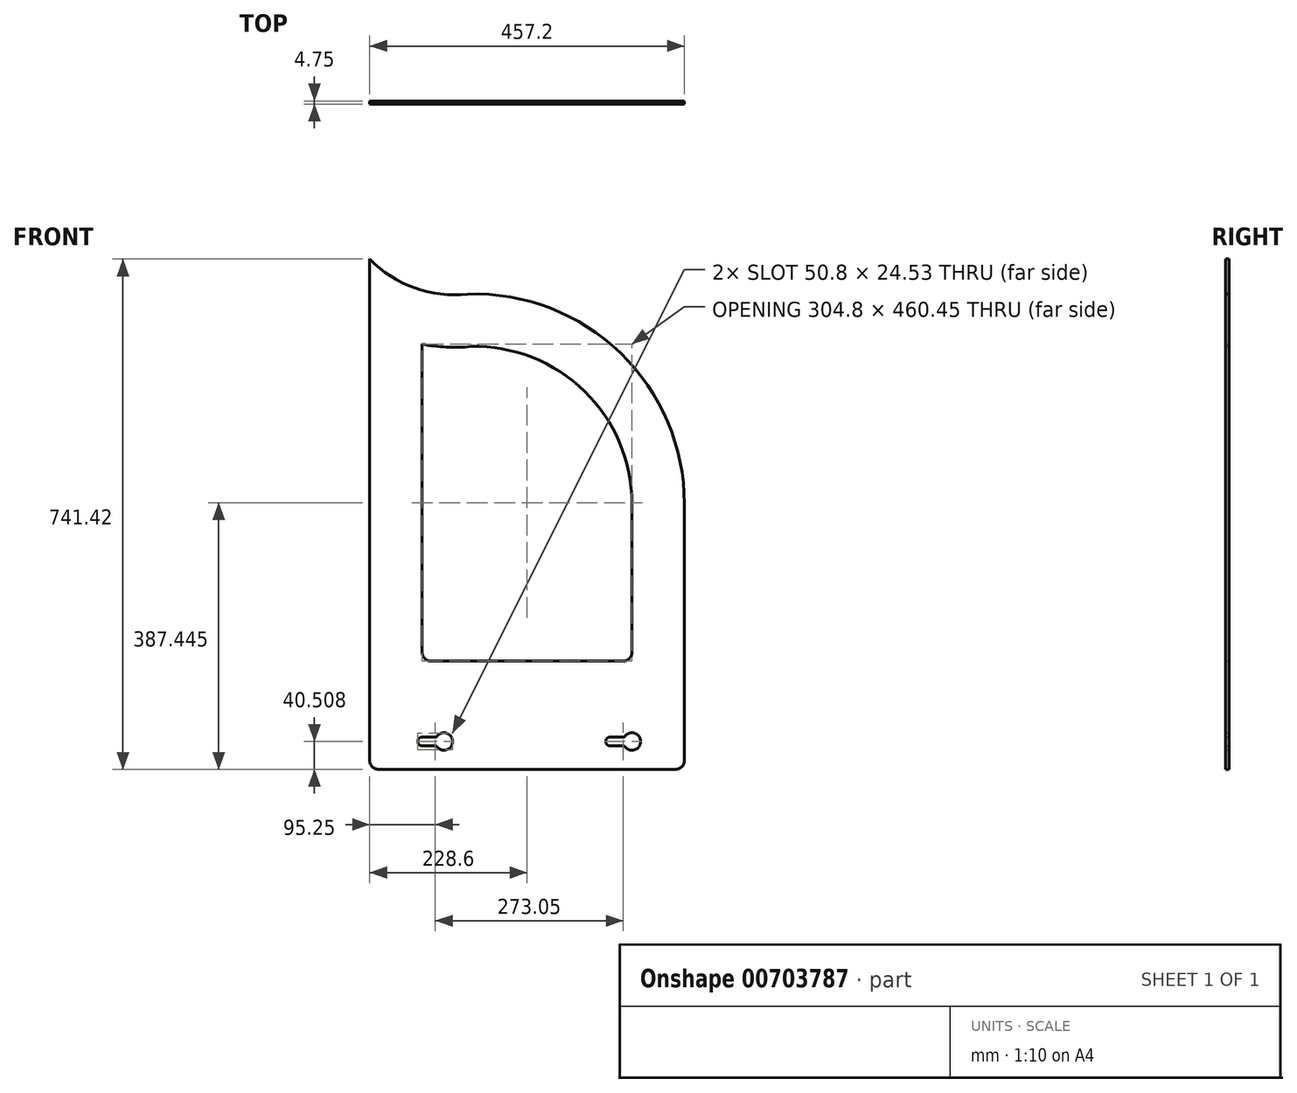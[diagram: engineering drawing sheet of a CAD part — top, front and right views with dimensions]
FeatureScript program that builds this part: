
annotation { "Feature Type Name" : "Feature", "Feature Type Description" : "" }
export const myFeature = defineFeature(function(context is Context, id is Id, definition is map)
    precondition{}
    {
        {
            var Q0;
            Q0=qCreatedBy(makeId("Front.planeOp"),FACE);
            var sketch = newSketch(context, id + "F0", { "sketchPlane" : qUnion([Q0])});
            skArc(sketch, "E0", {"start": v(304.8, 0) * mm, "mid": v(211.94, 219.05) * mm, "end": v(-10.05, 304.63) * mm});
            skLineSegment(sketch, "E1", {"start": v(304.8, 0) * mm, "end": v(304.8, -304.8) * mm});
            skLineSegment(sketch, "E2", {"start": v(304.8, -304.8) * mm, "end": v(0, -304.8) * mm});
            skLineSegment(sketch, "E3", {"start": v(0, -304.8) * mm, "end": v(-152.4, -304.8) * mm});
            skLineSegment(sketch, "E4", {"start": v(-152.4, -304.8) * mm, "end": v(-152.4, 355.6) * mm});
            skArc(sketch, "E5", {"start": v(-152.4, 355.6) * mm, "mid": v(-87.13, 313.61) * mm, "end": v(-10.05, 304.63) * mm});
            skArc(sketch, "E6.0", {"start": v(228.6, 0) * mm, "mid": v(159.86, 163.4) * mm, "end": v(-5.02, 228.54) * mm});
            skLineSegment(sketch, "E6.1", {"start": v(215.9, -228.6) * mm, "end": v(0, -228.6) * mm});
            skLineSegment(sketch, "E6.2", {"start": v(0, -228.6) * mm, "end": v(-63.5, -228.6) * mm});
            skLineSegment(sketch, "E6.3", {"start": v(228.6, 0) * mm, "end": v(228.6, -215.9) * mm});
            skLineSegment(sketch, "E6.4", {"start": v(-76.2, -215.9) * mm, "end": v(-76.2, 231.85) * mm});
            skArc(sketch, "E6.5", {"start": v(-76.2, 231.85) * mm, "mid": v(-40.73, 227.63) * mm, "end": v(-5.02, 228.54) * mm});
            skLineSegment(sketch, "E7", {"start": v(-152.4, -304.8) * mm, "end": v(-152.4, -373.12) * mm});
            skLineSegment(sketch, "E8", {"start": v(-139.7, -385.82) * mm, "end": v(292.1, -385.82) * mm});
            skLineSegment(sketch, "E9", {"start": v(304.8, -373.12) * mm, "end": v(304.8, -304.8) * mm});
            skArc(sketch, "E10", {"start": v(-55.45, -351.66) * mm, "mid": v(-31.75, -345.31) * mm, "end": v(-55.45, -338.96) * mm});
            skPoint(sketch, "E10.centerSnap0", {"position": v(-152.4, -345.31) * mm});
            skArc(sketch, "E11", {"start": v(217.6, -351.66) * mm, "mid": v(241.3, -345.31) * mm, "end": v(217.6, -338.96) * mm});
            skPoint(sketch, "E11.centerSnap0", {"position": v(304.8, -345.31) * mm});
            skArc(sketch, "E12", {"start": v(-76.2, -338.96) * mm, "mid": v(-82.55, -345.31) * mm, "end": v(-76.2, -351.66) * mm});
            skArc(sketch, "E13", {"start": v(196.85, -338.96) * mm, "mid": v(190.5, -345.31) * mm, "end": v(196.85, -351.66) * mm});
            skLineSegment(sketch, "E14", {"start": v(196.85, -338.96) * mm, "end": v(217.6, -338.96) * mm});
            skLineSegment(sketch, "E15", {"start": v(196.85, -351.66) * mm, "end": v(217.6, -351.66) * mm});
            skLineSegment(sketch, "E16", {"start": v(-76.2, -338.96) * mm, "end": v(-55.45, -338.96) * mm});
            skLineSegment(sketch, "E17", {"start": v(-76.2, -351.66) * mm, "end": v(-55.45, -351.66) * mm});
            skPoint(sketch, "E18.visualSharp", {"position": v(-152.4, -385.82) * mm});
            skArc(sketch, "E18.filletArc", {"start": v(-152.4, -373.12) * mm, "mid": v(-148.68, -382.1) * mm, "end": v(-139.7, -385.82) * mm});
            skPoint(sketch, "E19.visualSharp", {"position": v(-76.2, -228.6) * mm});
            skArc(sketch, "E19.filletArc", {"start": v(-76.2, -215.9) * mm, "mid": v(-72.48, -224.88) * mm, "end": v(-63.5, -228.6) * mm});
            skPoint(sketch, "E20.visualSharp", {"position": v(304.8, -385.82) * mm});
            skArc(sketch, "E20.filletArc", {"start": v(292.1, -385.82) * mm, "mid": v(301.08, -382.1) * mm, "end": v(304.8, -373.12) * mm});
            skPoint(sketch, "E21.visualSharp", {"position": v(228.6, -228.6) * mm});
            skArc(sketch, "E21.filletArc", {"start": v(215.9, -228.6) * mm, "mid": v(224.88, -224.88) * mm, "end": v(228.6, -215.9) * mm});
            skSolve(sketch);
        }
        {
            var Q0;
            Q0=makeQuery(id+"F0.imprint","IMPRINT",FACE,{"disambiguationData":[TD([[makeQuery(id+"F0.imprint","IMPRINT",EDGE,{"derivedFrom":sQuery(id+"F0.wireOp",EDGE,"E0")}),1.0]])]});
            var Q1;
            Q1=makeQuery(id+"F0.imprint","IMPRINT",FACE,{"disambiguationData":[TD([[makeQuery(id+"F0.imprint","IMPRINT",EDGE,{"derivedFrom":sQuery(id+"F0.wireOp",EDGE,"E2")}),1.0]])]});
            extrude(context, id + "F1", {"entities" : qUnion([Q0, Q1]), "depth" : 4.75 * mm, "offsetDistance" : 25.4 * mm});
        }
    });
